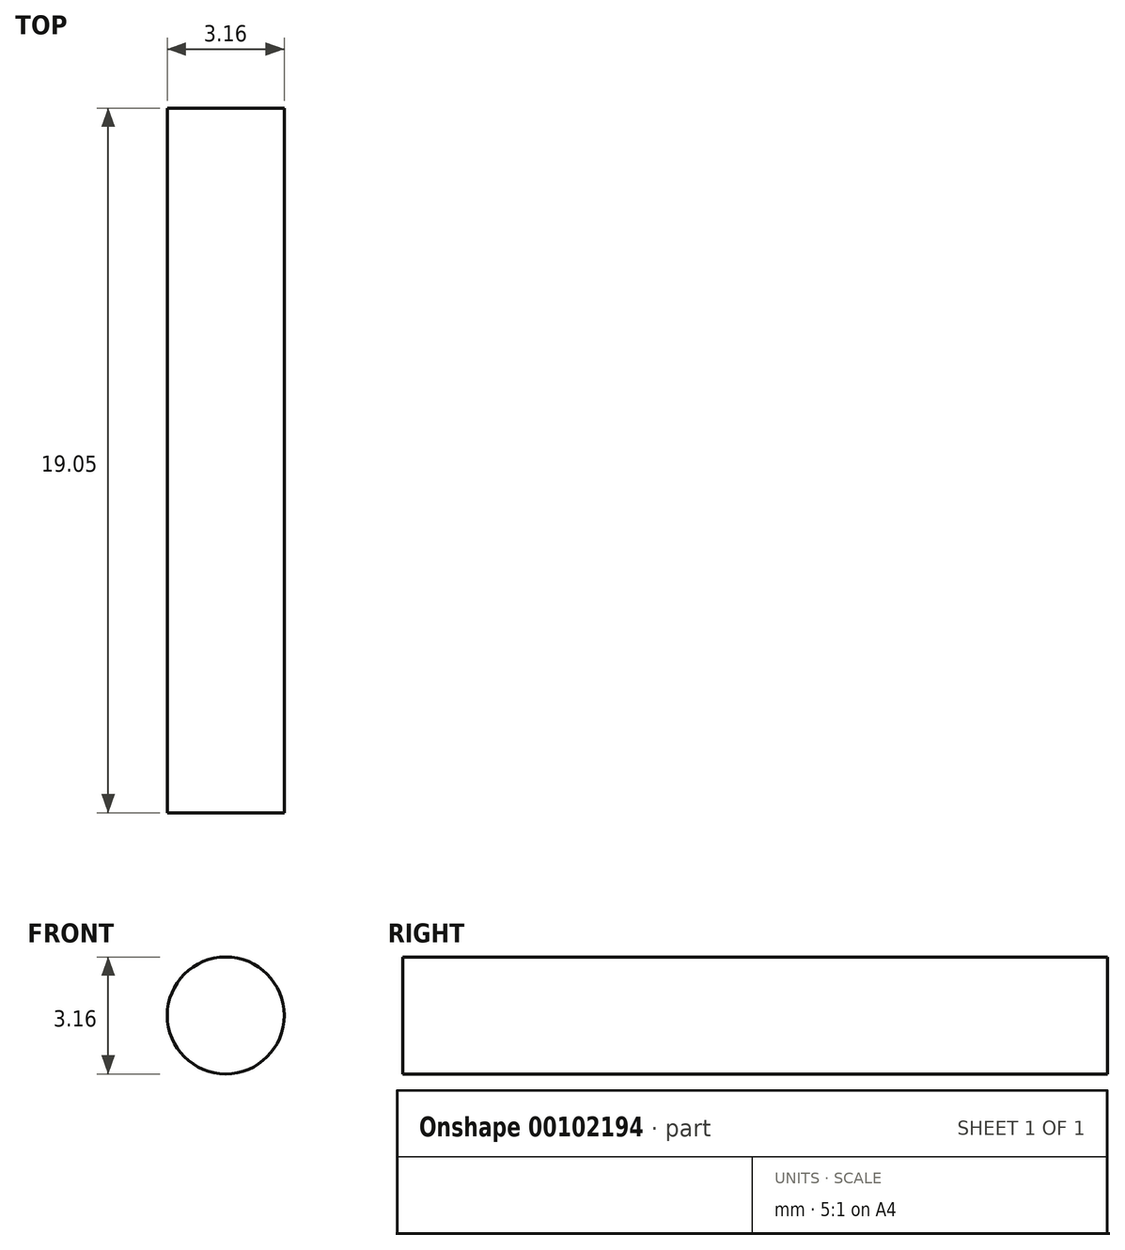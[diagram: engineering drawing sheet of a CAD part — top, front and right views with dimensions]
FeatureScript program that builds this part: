
annotation { "Feature Type Name" : "Feature", "Feature Type Description" : "" }
export const myFeature = defineFeature(function(context is Context, id is Id, definition is map)
    precondition{}
    {
        {
            var Q0;
            Q0=qCreatedBy(makeId("Front.planeOp"),FACE);
            var sketch = newSketch(context, id + "F0", { "sketchPlane" : qUnion([Q0])});
            skCircle(sketch, "E0", {"center": v(0, 0) * mm, "radius": 1.58 * mm});
            skSolve(sketch);
        }
        {
            var Q0;
            Q0=qSketchRegion(id+"F0",true);
            extrude(context, id + "F1", {"entities" : qUnion([Q0]), "depth" : 19.05 * mm});
        }
    });
